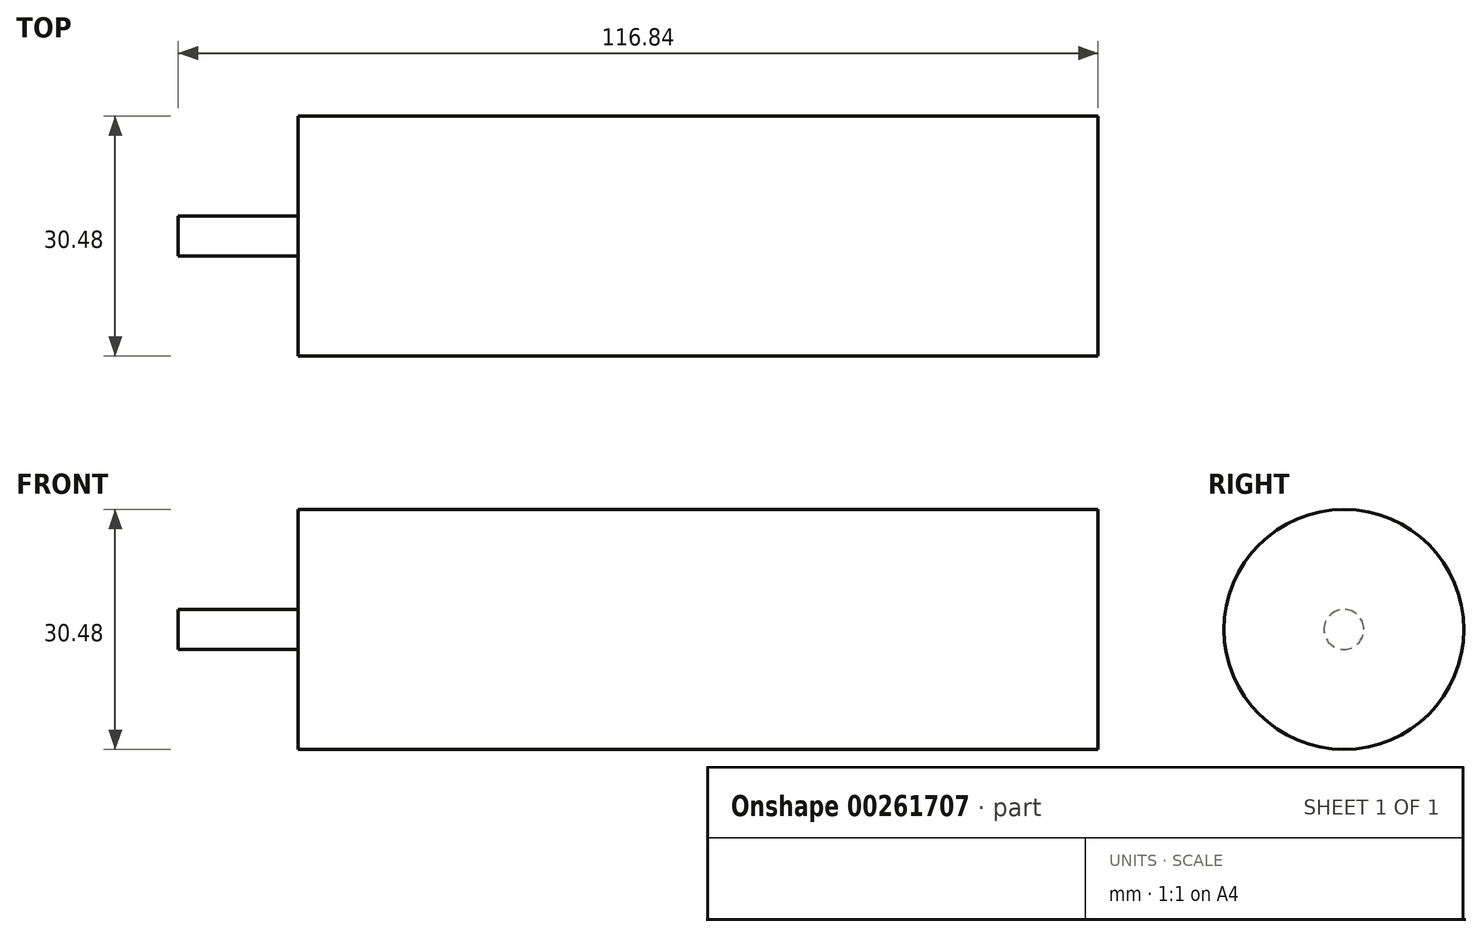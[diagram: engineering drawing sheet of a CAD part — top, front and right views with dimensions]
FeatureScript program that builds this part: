
annotation { "Feature Type Name" : "Feature", "Feature Type Description" : "" }
export const myFeature = defineFeature(function(context is Context, id is Id, definition is map)
    precondition{}
    {
        {
            var Q0;
            Q0=qCreatedBy(makeId("Front.planeOp"),FACE);
            var sketch = newSketch(context, id + "F0", { "sketchPlane" : qUnion([Q0])});
            skLineSegment(sketch, "E0.bottom", {"start": v(-101.6, 15.24) * mm, "end": v(0, 15.24) * mm});
            skLineSegment(sketch, "E0.top", {"start": v(-101.6, 0) * mm, "end": v(0, 0) * mm});
            skLineSegment(sketch, "E0.left", {"start": v(-101.6, 15.24) * mm, "end": v(-101.6, 0) * mm});
            skLineSegment(sketch, "E0.right", {"start": v(0, 15.24) * mm, "end": v(0, 0) * mm});
            skLineSegment(sketch, "E1.bottom", {"start": v(-101.6, 2.54) * mm, "end": v(-116.84, 2.54) * mm});
            skLineSegment(sketch, "E1.top", {"start": v(-101.6, 0) * mm, "end": v(-116.84, 0) * mm});
            skLineSegment(sketch, "E1.left", {"start": v(-101.6, 2.54) * mm, "end": v(-101.6, 0) * mm});
            skLineSegment(sketch, "E1.right", {"start": v(-116.84, 2.54) * mm, "end": v(-116.84, 0) * mm});
            skSolve(sketch);
        }
        {
            var Q0;
            Q0=makeQuery(id+"F0.imprint","IMPRINT",FACE,{"disambiguationData":[TD([[makeQuery(id+"F0.imprint","IMPRINT",EDGE,{"derivedFrom":sQuery(id+"F0.wireOp",EDGE,"E0.bottom")}),-1.0]])]});
            var Q1;
            Q1=makeQuery(id+"F0.imprint","IMPRINT",FACE,{"disambiguationData":[TD([[makeQuery(id+"F0.imprint","IMPRINT",EDGE,{"derivedFrom":sQuery(id+"F0.wireOp",EDGE,"4Mdd7Wrj-ERY2-7kqw-OsqN-ITfqLy4fsuE3.bottom")}),-1.0]])]});
            var Q2;
            Q2=makeQuery(id+"F0.imprint","IMPRINT",FACE,{"disambiguationData":[TD([[makeQuery(id+"F0.imprint","IMPRINT",EDGE,{"derivedFrom":sQuery(id+"F0.wireOp",EDGE,"E1.bottom")}),1.0]])]});
            var Q3;
            Q3=sQuery(id+"F0.wireOp",EDGE,"E0.top");
            revolve(context, id + "F1", {"entities" : qUnion([Q0, Q1, Q2]), "axis" : qUnion([Q3]), "revolveType" : RevolveType.FULL});
        }
    });
